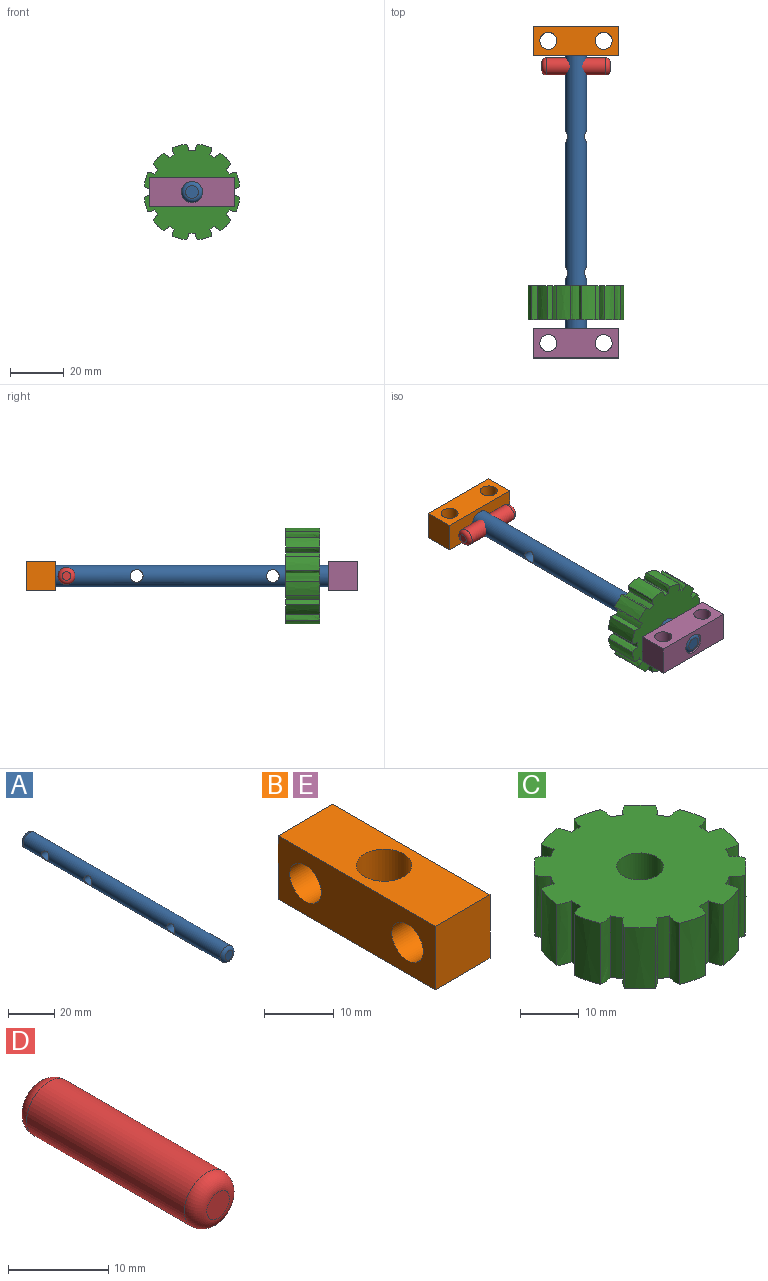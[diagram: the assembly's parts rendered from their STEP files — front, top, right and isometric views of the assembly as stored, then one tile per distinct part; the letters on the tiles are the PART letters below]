
ASSEMBLY  parts=5 mates=4
PART A: 8 faces, bbox 8.6x123.8x8.6 mm
  f0: cylinder r=3.97mm len=120.65mm, axis (0,1,0), area 2896.2mm2, adj f3,f4,f5,f6,f7
  f1: plane 4.76x4.76mm, normal (0,-1,0), area 17.8mm2, adj f4
  f2: plane 4.76x4.76mm, normal (0,1,0), area 17.8mm2, adj f3
  f3: torus R=2.38mm, axis (0,-1,0), area 53.1mm2, adj f0,f2
  f4: torus R=2.38mm, axis (0,-1,0), area 53.1mm2, adj f0,f1
  f5: cylinder r=2.38mm len=7.94mm, axis (1,0,0), area 107.2mm2, adj f0
  f6: cylinder r=2.38mm len=7.94mm, axis (1,0,0), area 107.2mm2, adj f0
  f7: cylinder r=2.38mm len=7.94mm, axis (1,0,0), area 107.2mm2, adj f0
PART B: 9 faces, bbox 11.1x31.8x11.1 mm
  f0: plane 31.75x11.11mm, normal (-1,0,0), area 289.5mm2, adj f1,f3,f4,f5,f7,f8
  f1: plane 31.75x11.11mm, normal (0,0,-1), area 303.3mm2, adj f0,f2,f4,f5,f6
  f2: plane 31.75x11.11mm, normal (1,0,0), area 289.5mm2, adj f1,f3,f4,f5,f7,f8
  f3: plane 31.75x11.11mm, normal (0,0,1), area 303.3mm2, adj f0,f2,f4,f5,f6
  f4: plane 11.11x11.11mm, normal (0,-1,0), area 123.5mm2, adj f0,f1,f2,f3
  f5: plane 11.11x11.11mm, normal (0,1,0), area 123.5mm2, adj f0,f1,f2,f3
  f6: cylinder r=3.97mm len=11.11mm, axis (0,0,1), area 277.1mm2, adj f1,f3
  f7: cylinder r=3.17mm len=11.11mm, axis (1,0,0), area 221.7mm2, adj f0,f2
  f8: cylinder r=3.17mm len=11.11mm, axis (1,0,0), area 221.7mm2, adj f0,f2
PART C: 51 faces, bbox 35.8x35.8x12.7 mm
  f0: extruded ~12.7x2.07mm, area 34.4mm2, adj f1,f47,f48,f49
  f1: extruded ~12.7x3.7mm, area 66.6mm2, adj f0,f2,f48,f49
  f2: extruded ~12.7x2.07mm, area 34.4mm2, adj f1,f3,f48,f49
  f3: extruded ~12.7x1.97mm, area 29mm2, adj f2,f4,f48,f49
  f4: extruded ~12.7x2.63mm, area 34.4mm2, adj f3,f5,f48,f49
  f5: extruded ~12.7x5.05mm, area 66.6mm2, adj f4,f6,f48,f49
  f6: extruded ~12.7x2.5mm, area 34.4mm2, adj f5,f7,f48,f49
  f7: extruded ~12.7x2.28mm, area 29mm2, adj f6,f8,f48,f49
  f8: extruded ~12.7x2.5mm, area 34.4mm2, adj f7,f9,f48,f49
  f9: extruded ~12.7x5.05mm, area 66.6mm2, adj f8,f10,f48,f49
  f10: extruded ~12.7x2.63mm, area 34.4mm2, adj f9,f11,f48,f49
  f11: extruded ~12.7x1.97mm, area 29mm2, adj f10,f12,f48,f49
  f12: extruded ~12.7x2.07mm, area 34.4mm2, adj f11,f13,f48,f49
  f13: extruded ~12.7x3.7mm, area 66.6mm2, adj f12,f14,f48,f49
  f14: extruded ~12.7x2.07mm, area 34.4mm2, adj f13,f15,f48,f49
  f15: extruded ~12.7x1.97mm, area 29mm2, adj f14,f16,f48,f49
  f16: extruded ~12.7x2.63mm, area 34.4mm2, adj f15,f17,f48,f49
  f17: extruded ~12.7x5.05mm, area 66.6mm2, adj f16,f18,f48,f49
  f18: extruded ~12.7x2.5mm, area 34.4mm2, adj f17,f19,f48,f49
  f19: extruded ~12.7x2.28mm, area 29mm2, adj f18,f20,f48,f49
  f20: extruded ~12.7x2.5mm, area 34.4mm2, adj f19,f21,f48,f49
  f21: extruded ~12.7x5.05mm, area 66.6mm2, adj f20,f22,f48,f49
  f22: extruded ~12.7x2.63mm, area 34.4mm2, adj f21,f23,f48,f49
  f23: extruded ~12.7x1.97mm, area 29mm2, adj f22,f24,f48,f49
  f24: extruded ~12.7x2.07mm, area 34.4mm2, adj f23,f25,f48,f49
  f25: extruded ~12.7x3.7mm, area 66.6mm2, adj f24,f26,f48,f49
  f26: extruded ~12.7x2.07mm, area 34.4mm2, adj f25,f27,f48,f49
  f27: extruded ~12.7x1.97mm, area 29mm2, adj f26,f28,f48,f49
  f28: extruded ~12.7x2.63mm, area 34.4mm2, adj f27,f29,f48,f49
  f29: extruded ~12.7x5.05mm, area 66.6mm2, adj f28,f30,f48,f49
  f30: extruded ~12.7x2.5mm, area 34.4mm2, adj f29,f31,f48,f49
  f31: extruded ~12.7x2.28mm, area 29mm2, adj f30,f32,f48,f49
  f32: extruded ~12.7x2.5mm, area 34.4mm2, adj f31,f33,f48,f49
  f33: extruded ~12.7x5.05mm, area 66.6mm2, adj f32,f34,f48,f49
  f34: extruded ~12.7x2.63mm, area 34.4mm2, adj f33,f35,f48,f49
  f35: extruded ~12.7x1.97mm, area 29mm2, adj f34,f36,f48,f49
  f36: extruded ~12.7x2.07mm, area 34.4mm2, adj f35,f37,f48,f49
  f37: extruded ~12.7x3.7mm, area 66.6mm2, adj f36,f38,f48,f49
  f38: extruded ~12.7x2.07mm, area 34.4mm2, adj f37,f39,f48,f49
  f39: extruded ~12.7x1.97mm, area 29mm2, adj f38,f40,f48,f49
  f40: extruded ~12.7x2.63mm, area 34.4mm2, adj f39,f41,f48,f49
  f41: extruded ~12.7x5.05mm, area 66.6mm2, adj f40,f42,f48,f49
  f42: extruded ~12.7x2.5mm, area 34.4mm2, adj f41,f43,f48,f49
  f43: extruded ~12.7x2.28mm, area 29mm2, adj f42,f44,f48,f49
  f44: extruded ~12.7x2.5mm, area 34.4mm2, adj f43,f45,f48,f49
  f45: extruded ~12.7x5.05mm, area 66.6mm2, adj f44,f46,f48,f49
  f46: extruded ~12.7x2.63mm, area 34.4mm2, adj f45,f47,f48,f49
  f47: extruded ~12.7x1.97mm, area 29mm2, adj f0,f46,f48,f49
  f48: plane 35.76x35.76mm, normal (0,0,-1), area 876.8mm2, adj f0,f1,f2,f3,f4,f5,f6,f7
  f49: plane 35.76x35.76mm, normal (0,0,1), area 876.8mm2, adj f0,f1,f2,f3,f4,f5,f6,f7
  f50: cylinder r=3.97mm len=12.7mm, axis (0,0,1), area 316.7mm2, adj f48,f49
PART D: 5 faces, bbox 6.9x25.4x6.9 mm
  f0: cylinder r=3.17mm len=22.23mm, axis (0,1,0), area 443.4mm2, adj f3,f4
  f1: plane 3.18x3.18mm, normal (0,-1,0), area 7.9mm2, adj f4
  f2: plane 3.18x3.18mm, normal (0,1,0), area 7.9mm2, adj f3
  f3: torus R=1.59mm, axis (0,-1,0), area 40.7mm2, adj f0,f2
  f4: torus R=1.59mm, axis (0,-1,0), area 40.7mm2, adj f0,f1
PART E: same geometry as B
PLACE A t=(-29.4,31.78,-19.75)mm fixed
PLACE B rot(axis=(-0.58,0.58,0.58),120deg) t=(-45.27,20.66,-14.19)mm
PLACE C rot(axis=(-1,0,0),90deg) t=(-29.4,-65.06,-19.75)mm
PLACE D rot(axis=(0.58,0.58,-0.58),120deg) t=(-16.7,16.69,-19.75)mm
PLACE E rot(axis=(0.58,-0.58,0.58),120deg) t=(-45.27,-80.94,-25.3)mm
MATE fastened C.f50 <-> A.f0  axis (0,1,0) through (-29.4,-65.06,-19.75)mm
MATE revolute B.f6 <-> A.f0  axis (0,1,0) through (-29.4,31.78,-19.75)mm
MATE revolute E.f6 <-> A.f0  axis (0,-1,0) through (-29.4,-92.05,-19.75)mm
MATE fastened D.f0 <-> A.f7  axis (1,0,0) through (-29.4,16.69,-19.75)mm
